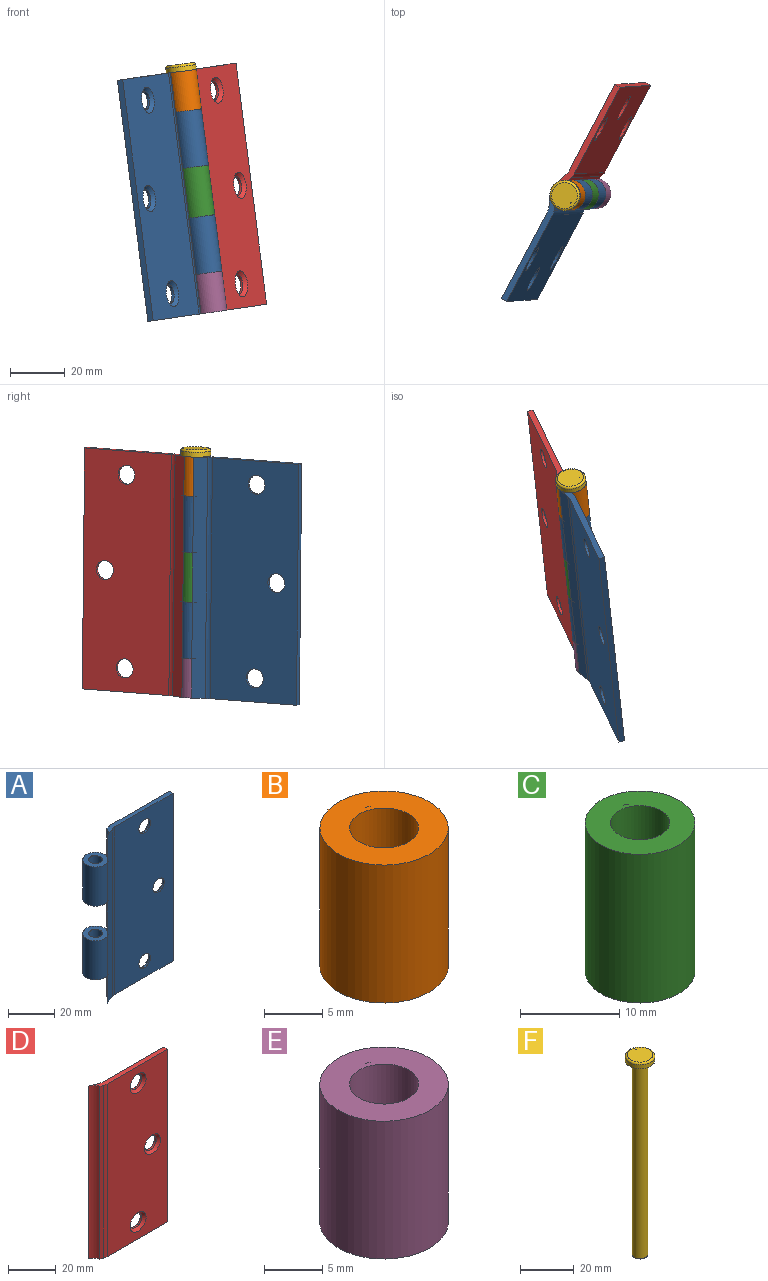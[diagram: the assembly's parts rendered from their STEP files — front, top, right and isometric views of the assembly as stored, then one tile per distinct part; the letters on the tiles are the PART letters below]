
ASSEMBLY  parts=6 mates=8
PART A: 30 faces, bbox 50x11.1x88.9 mm
  f0: cylinder r=5.53mm len=18.31mm, axis (0,0,1), area 90.4mm2, adj f2,f3,f14,f20
  f1: cylinder r=5.53mm len=14.55mm, axis (0,0,1), area 71.9mm2, adj f2,f3,f7,f15
  f2: plane 88.9x1.48mm, normal (-0.36,0.93,0), area 140.7mm2, adj f0,f1,f7,f8,f9,f13,f17,f29
  f3: plane 88.9x4.76mm, normal (0.36,-0.93,0), area 453.2mm2, adj f0,f1,f7,f8,f9,f13,f17,f28
  f4: plane 88.9x35.89mm, normal (0,-1,0), area 3074.7mm2, adj f5,f7,f8,f22,f23,f24,f28
  f5: plane 88.9x2.21mm, normal (1,0,0), area 196.5mm2, adj f4,f6,f7,f8
  f6: plane 88.9x35.89mm, normal (0,1,0), area 2975.6mm2, adj f5,f7,f8,f25,f26,f27,f29
  f7: plane 42.47x4.37mm, normal (0,0,1), area 88.5mm2, adj f1,f2,f3,f4,f5,f6,f28,f29
  f8: plane 42.47x4.37mm, normal (0,0,-1), area 88.5mm2, adj f2,f3,f4,f5,f6,f9,f28,f29
  f9: cylinder r=5.53mm len=14.5mm, axis (0,0,1), area 71.6mm2, adj f2,f3,f8,f21
  f10: cylinder r=3.47mm len=20.75mm, axis (0,0,1), area 9.5mm2, adj f11,f14,f15
  f11: plane 20.75x0.43mm, normal (0.36,0.93,0), area 9.5mm2, adj f10,f14,f15
  f12: cylinder r=2.97mm len=20.75mm, axis (0,0,1), area 387.5mm2, adj f14,f15
  f13: cylinder r=5.53mm len=20.75mm, axis (0,0,1), area 618.4mm2, adj f2,f3,f14,f15
  f14: plane 11.06x11.06mm, normal (0,0,-1), area 68.3mm2, adj f0,f10,f11,f12,f13
  f15: plane 11.06x11.06mm, normal (0,0,1), area 68.3mm2, adj f1,f10,f11,f12,f13
  f16: plane 20.78x0.43mm, normal (0.36,0.93,0), area 9.5mm2, adj f18,f20,f21
  f17: cylinder r=5.53mm len=20.78mm, axis (0,0,-1), area 619.2mm2, adj f2,f3,f20,f21
  f18: cylinder r=3.47mm len=20.78mm, axis (0,0,-1), area 9.5mm2, adj f16,f20,f21
  f19: cylinder r=2.97mm len=20.78mm, axis (0,0,-1), area 388mm2, adj f20,f21
  f20: plane 11.06x11.06mm, normal (0,0,1), area 68.3mm2, adj f0,f16,f17,f18,f19
  f21: plane 11.06x11.06mm, normal (0,0,-1), area 68.3mm2, adj f9,f16,f17,f18,f19
  f22: cylinder r=3.51mm len=7.01mm, axis (0,1,0), area 20.7mm2, adj f4,f26
  f23: cylinder r=3.51mm len=7.01mm, axis (0,1,0), area 20.7mm2, adj f4,f27
  f24: cylinder r=3.51mm len=7.01mm, axis (0,1,0), area 20.7mm2, adj f4,f25
  f25: cone r=3.51mm half-angle=45deg, axis (0,1,0), area 46.7mm2, adj f6,f24
  f26: cone r=3.51mm half-angle=45deg, axis (0,1,0), area 46.7mm2, adj f6,f22
  f27: cone r=3.51mm half-angle=45deg, axis (0,1,0), area 46.7mm2, adj f6,f23
  f28: cylinder r=5.08mm len=88.9mm, axis (0,0,1), area 165.5mm2, adj f3,f4,f7,f8
  f29: cylinder r=5.08mm len=88.9mm, axis (0,0,1), area 165.5mm2, adj f2,f6,f7,f8
PART B: 6 faces, bbox 11.1x11.1x14.6 mm
  f0: cylinder r=3.47mm len=14.55mm, axis (0,0,1), area 6.7mm2, adj f1,f4,f5
  f1: plane 14.55x0.43mm, normal (0.36,0.93,0), area 6.7mm2, adj f0,f4,f5
  f2: cylinder r=2.97mm len=14.55mm, axis (0,0,1), area 271.8mm2, adj f4,f5
  f3: cylinder r=5.53mm len=14.55mm, axis (0,0,1), area 505.6mm2, adj f4,f5
  f4: plane 11.06x11.06mm, normal (0,0,-1), area 68.3mm2, adj f0,f1,f2,f3
  f5: plane 11.06x11.06mm, normal (0,0,1), area 68.3mm2, adj f0,f1,f2,f3
PART C: 6 faces, bbox 11.1x11.1x18.3 mm
  f0: cylinder r=3.47mm len=18.31mm, axis (0,0,1), area 8.4mm2, adj f1,f4,f5
  f1: plane 18.31x0.43mm, normal (0.36,0.93,0), area 8.4mm2, adj f0,f4,f5
  f2: cylinder r=2.97mm len=18.31mm, axis (0,0,1), area 342mm2, adj f4,f5
  f3: cylinder r=5.53mm len=18.31mm, axis (0,0,1), area 636.2mm2, adj f4,f5
  f4: plane 11.06x11.06mm, normal (0,0,-1), area 68.3mm2, adj f0,f1,f2,f3
  f5: plane 11.06x11.06mm, normal (0,0,1), area 68.3mm2, adj f0,f1,f2,f3
PART D: 16 faces, bbox 42.5x4.4x88.9 mm
  f0: plane 88.9x4.76mm, normal (0.36,0.93,0), area 453.3mm2, adj f5,f6,f7,f15
  f1: plane 88.9x1.48mm, normal (-0.36,-0.93,0), area 140.7mm2, adj f5,f6,f7,f14
  f2: plane 88.9x35.89mm, normal (0,-1,0), area 2975.8mm2, adj f3,f5,f6,f11,f12,f13,f14
  f3: plane 88.9x2.22mm, normal (1,0,0), area 197.1mm2, adj f2,f4,f5,f6
  f4: plane 88.9x35.89mm, normal (0,1,0), area 3074.9mm2, adj f3,f5,f6,f8,f9,f10,f15
  f5: plane 42.47x4.37mm, normal (0,0,1), area 88.8mm2, adj f0,f1,f2,f3,f4,f7,f14,f15
  f6: plane 42.47x4.37mm, normal (0,0,-1), area 88.8mm2, adj f0,f1,f2,f3,f4,f7,f14,f15
  f7: cylinder r=5.53mm len=88.9mm, axis (0,0,1), area 439.4mm2, adj f0,f1,f5,f6
  f8: cylinder r=3.51mm len=7.01mm, axis (0,-1,0), area 20.9mm2, adj f4,f13
  f9: cylinder r=3.51mm len=7.01mm, axis (0,-1,0), area 20.9mm2, adj f4,f11
  f10: cylinder r=3.51mm len=7.01mm, axis (0,-1,0), area 20.9mm2, adj f4,f12
  f11: cone r=3.51mm half-angle=45deg, axis (0,-1,0), area 46.7mm2, adj f2,f9
  f12: cone r=3.51mm half-angle=45deg, axis (0,-1,0), area 46.7mm2, adj f2,f10
  f13: cone r=3.51mm half-angle=45deg, axis (0,-1,0), area 46.7mm2, adj f2,f8
  f14: cylinder r=5.08mm len=88.9mm, axis (0,0,-1), area 165mm2, adj f1,f2,f5,f6
  f15: cylinder r=5.08mm len=88.9mm, axis (0,0,-1), area 165mm2, adj f0,f4,f5,f6
PART E: 6 faces, bbox 11.1x11.1x14.5 mm
  f0: plane 14.5x0.43mm, normal (0.36,0.93,0), area 6.6mm2, adj f2,f4,f5
  f1: cylinder r=5.53mm len=14.5mm, axis (0,0,1), area 503.8mm2, adj f4,f5
  f2: cylinder r=3.47mm len=14.5mm, axis (0,0,1), area 6.6mm2, adj f0,f4,f5
  f3: cylinder r=2.97mm len=14.5mm, axis (0,0,1), area 270.8mm2, adj f4,f5
  f4: plane 11.06x11.06mm, normal (0,0,-1), area 68.3mm2, adj f0,f1,f2,f3
  f5: plane 11.06x11.06mm, normal (0,0,1), area 68.3mm2, adj f0,f1,f2,f3
PART F: 9 faces, bbox 12x12x91.4 mm
  f0: cylinder r=3.47mm len=2.54mm, axis (0,0,-1), area 1.2mm2, adj f1,f3,f4
  f1: plane 2.54x0.43mm, normal (0.36,0.93,0), area 1.2mm2, adj f0,f3,f4
  f2: cylinder r=5.53mm len=11.06mm, axis (0,0,-1), area 61.8mm2, adj f4,f5
  f3: plane 9.53x9.53mm, normal (0,0,1), area 71.4mm2, adj f0,f1,f5
  f4: plane 11.06x11.06mm, normal (0,0,-1), area 68.3mm2, adj f0,f1,f2,f6
  f5: torus R=4.77mm, axis (0,0,1), area 39.5mm2, adj f2,f3
  f6: cylinder r=2.97mm len=88.65mm, axis (0,0,1), area 1655.2mm2, adj f4,f8
  f7: plane 5.44x5.44mm, normal (0,0,-1), area 23.2mm2, adj f8
  f8: cone r=2.97mm half-angle=45deg, axis (0,0,1), area 6.4mm2, adj f6,f7
PLACE A rot(axis=(0.07,-0.03,-1),118.3deg) t=(43.21,52.98,-121.02)mm
PLACE B rot(axis=(-0.05,-0.11,0.99),62.3deg) t=(-96.36,27.99,-138.94)mm
PLACE C rot(axis=(-0.05,-0.11,0.99),62.3deg) t=(-96.36,27.99,-138.93)mm
PLACE D rot(axis=(-0.05,-0.11,0.99),62.3deg) t=(-96.36,27.99,-138.94)mm
PLACE E rot(axis=(-0.05,-0.11,0.99),62.3deg) t=(-96.36,27.99,-138.94)mm
PLACE F rot(axis=(0.07,-0.03,-1),118.2deg) t=(43.19,53.09,-121.02)mm
MATE pin_slot F.f0 <-> B.f0  axis (0.13,0.01,-0.99) through (-37.76,39.69,-41.79)mm
MATE revolute A.f0 <-> B.f0  axis (-0.13,-0.01,0.99) through (-35.93,39.83,-56.23)mm
MATE pin_slot B.f0 <-> F.f0  axis (-0.13,-0.01,0.99) through (-37.76,39.69,-41.79)mm
MATE cylindrical F.f0 <-> B.f0  axis (-0.13,-0.01,0.99) through (-37.76,39.69,-41.79)mm
MATE fastened B.f0 <-> D.f7  axis (-0.13,-0.01,0.99) through (-37.76,39.69,-41.79)mm
MATE fastened D.f7 <-> C.f0  axis (-0.13,-0.01,0.99) through (-32.17,40.12,-85.89)mm
MATE fastened E.f1 <-> D.f7  axis (0.13,0.01,-0.99) through (-26.58,40.54,-129.98)mm
MATE slider F.f0 <-> C.f0  axis (-0.13,-0.01,0.99) through (-32.19,40.12,-85.76)mm
